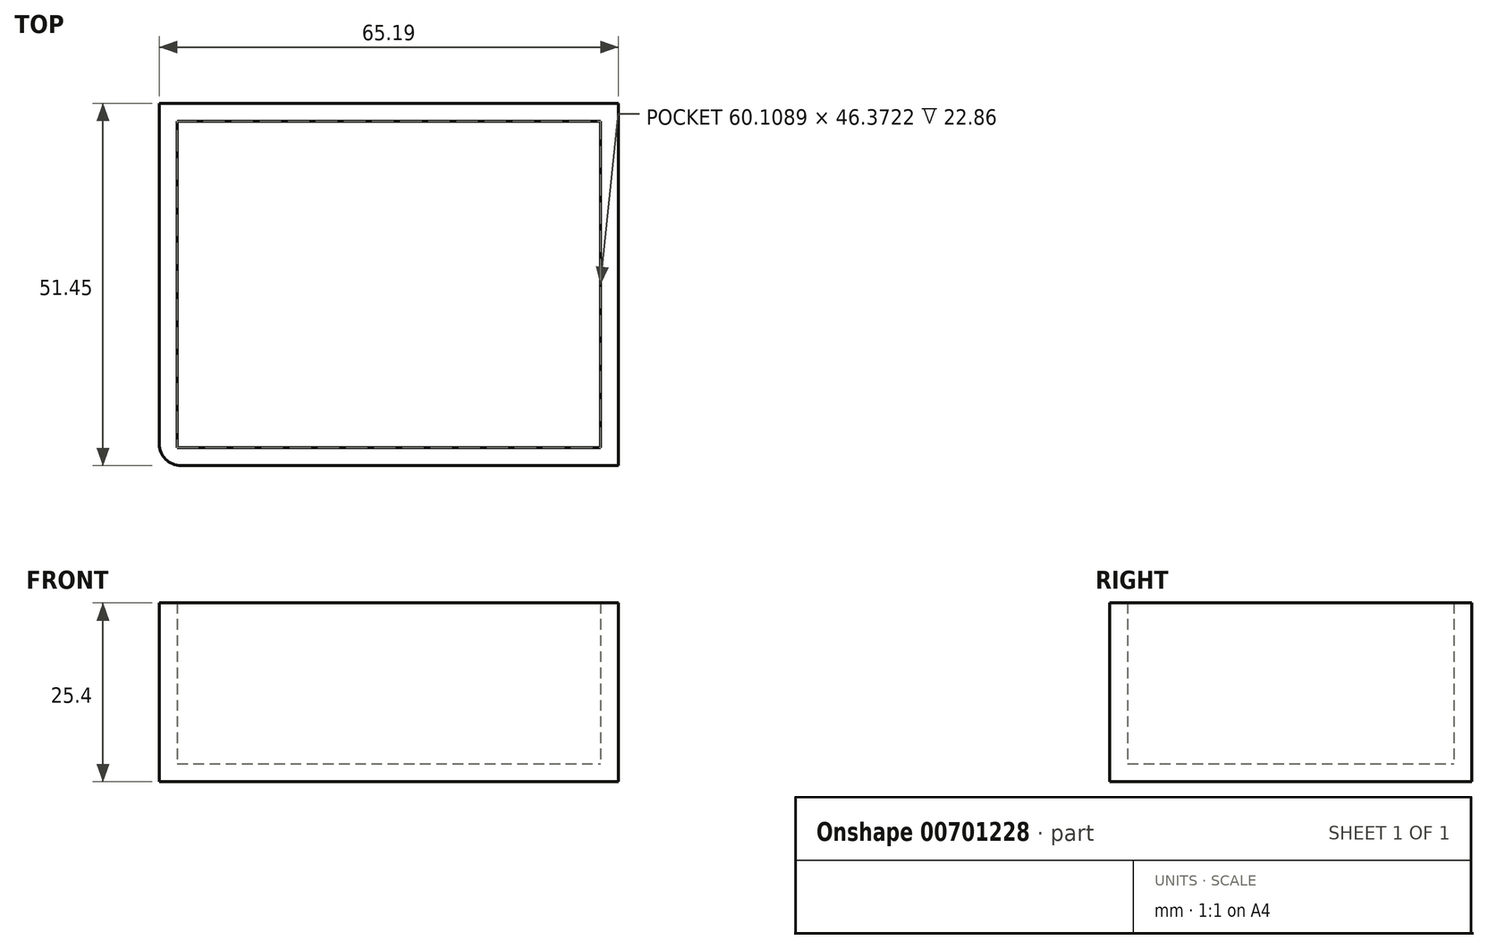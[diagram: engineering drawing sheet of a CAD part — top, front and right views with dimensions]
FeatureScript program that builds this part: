
annotation { "Feature Type Name" : "Feature", "Feature Type Description" : "" }
export const myFeature = defineFeature(function(context is Context, id is Id, definition is map)
    precondition{}
    {
        {
            var Q0;
            Q0=qCreatedBy(makeId("Top.planeOp"),FACE);
            var sketch = newSketch(context, id + "F0", { "sketchPlane" : qUnion([Q0])});
            skLineSegment(sketch, "E0.bottom", {"start": v(0, 0) * mm, "end": v(65.19, 0) * mm});
            skLineSegment(sketch, "E0.top", {"start": v(0, 51.45) * mm, "end": v(65.19, 51.45) * mm});
            skLineSegment(sketch, "E0.left", {"start": v(0, 0) * mm, "end": v(0, 51.45) * mm});
            skLineSegment(sketch, "E0.right", {"start": v(65.19, 0) * mm, "end": v(65.19, 51.45) * mm});
            skSolve(sketch);
        }
        {
            var Q0;
            Q0 = qSketchRegion(id + "F0", true);
            extrude(context, id + "F1", {"entities" : qUnion([Q0]), "depth" : 25.4 * mm, "offsetDistance" : 25.4 * mm});
        }
        {
            var Q0;
            Q0=makeQuery(id+"F1.opExtrude","CAP_FACE",FACE,{"disambiguationData":[OSD([sQuery(id+"F0.wireOp",EDGE,"E0.bottom"),sQuery(id+"F0.wireOp",EDGE,"E0.top"),sQuery(id+"F0.wireOp",EDGE,"E0.left"),sQuery(id+"F0.wireOp",EDGE,"E0.right")])],"isStart":false});
            shell(context, id + "F2", {"entities" : qUnion([Q0]), "thickness" : 25.4 * mm});
        }
        {
            var Q0;
            Q0=makeQuery(id+"F1.opExtrude","CAP_FACE",FACE,{"disambiguationData":[OSD([sQuery(id+"F0.wireOp",EDGE,"E0.bottom"),sQuery(id+"F0.wireOp",EDGE,"E0.top"),sQuery(id+"F0.wireOp",EDGE,"E0.left"),sQuery(id+"F0.wireOp",EDGE,"E0.right")])],"isStart":false});
            shell(context, id + "F3", {"entities" : qUnion([Q0]), "thickness" : 2.54 * mm});
        }
        {
            var Q0;
            Q0=makeQuery(id+"F1.opExtrude","SWEPT_EDGE",EDGE,{"disambiguationData":[OSD([sQuery(id+"F0.wireOp",EDGE,"E0.bottom"),sQuery(id+"F0.wireOp",EDGE,"E0.left")])]});
            fillet(context, id + "F4", {"entities" : qUnion([Q0]), "radius" : 3.07 * mm, "tangentPropagation" : true, "allowEdgeOverflow" : false});
        }
    });
